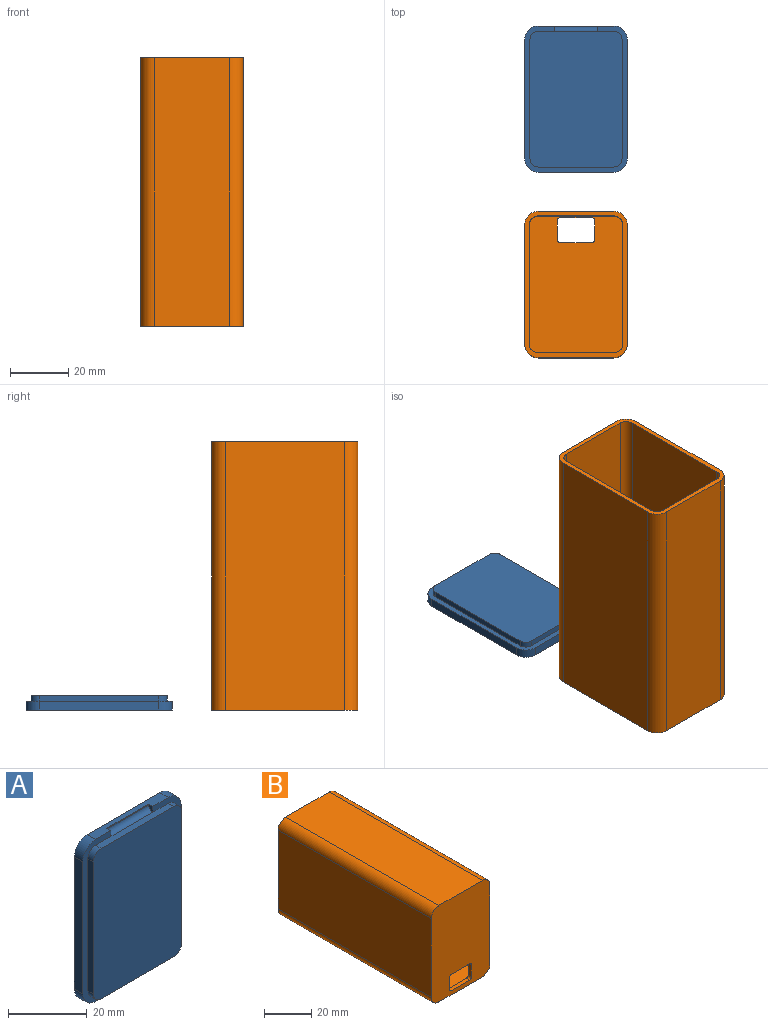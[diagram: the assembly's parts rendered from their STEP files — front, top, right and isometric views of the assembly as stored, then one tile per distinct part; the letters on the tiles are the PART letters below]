
ASSEMBLY  parts=2 mates=2
PART A: 23 faces, bbox 35.2x5x50.2 mm
  f0: plane 50.2x35.2mm, normal (0,-1,0), area 256mm2, adj f1,f2,f3,f4,f5,f6,f7,f8
  f1: plane 26x3mm, normal (0,0,1), area 55.5mm2, adj f0,f2,f8,f9,f19,f20,f21
  f2: cylinder r=4.6mm len=4.6mm, axis (0,-1,0), area 21.7mm2, adj f0,f1,f3,f9
  f3: plane 41x3mm, normal (1,0,0), area 123mm2, adj f0,f2,f4,f9
  f4: cylinder r=4.6mm len=4.6mm, axis (0,-1,0), area 21.7mm2, adj f0,f3,f5,f9
  f5: plane 26x3mm, normal (0,0,-1), area 78mm2, adj f0,f4,f6,f9
  f6: cylinder r=4.6mm len=4.6mm, axis (0,-1,0), area 21.7mm2, adj f0,f5,f7,f9
  f7: plane 41x3mm, normal (-1,0,0), area 123mm2, adj f0,f6,f8,f9
  f8: cylinder r=4.6mm len=4.6mm, axis (0,-1,0), area 21.7mm2, adj f0,f1,f7,f9
  f9: plane 50.2x35.2mm, normal (0,1,0), area 1748.9mm2, adj f1,f2,f3,f4,f5,f6,f7,f8
  f10: plane 41x2mm, normal (1,0,0), area 82mm2, adj f0,f11,f17,f18
  f11: cylinder r=2.8mm len=2.8mm, axis (0,1,0), area 8.8mm2, adj f0,f10,f12,f18
  f12: plane 26x2mm, normal (0,0,-1), area 52mm2, adj f0,f11,f13,f18
  f13: cylinder r=2.8mm len=2.8mm, axis (0,1,0), area 8.8mm2, adj f0,f12,f14,f18
  f14: plane 41x2mm, normal (-1,0,0), area 82mm2, adj f0,f13,f15,f18
  f15: cylinder r=2.8mm len=2.8mm, axis (0,1,0), area 8.8mm2, adj f0,f14,f16,f18
  f16: plane 26x2mm, normal (0,0,1), area 52mm2, adj f0,f15,f17,f18,f22
  f17: cylinder r=2.8mm len=2.8mm, axis (0,1,0), area 8.8mm2, adj f0,f10,f16,f18
  f18: plane 46.6x31.6mm, normal (0,-1,0), area 1465.8mm2, adj f10,f11,f12,f13,f14,f15,f16,f17
  f19: plane 1.8x1.5mm, normal (1,0,0), area 2.2mm2, adj f0,f1,f21,f22
  f20: plane 1.8x1.5mm, normal (-1,0,0), area 2.2mm2, adj f0,f1,f21,f22
  f21: plane 15x0.3mm, normal (0,-1,0), area 4.5mm2, adj f1,f19,f20,f22
  f22: cylinder r=1.5mm len=15mm, axis (1,0,0), area 35.3mm2, adj f16,f19,f20,f21
PART B: 27 faces, bbox 35.2x92x50.2 mm
  f0: plane 92x26mm, normal (0,0,1), area 2392mm2, adj f1,f15,f16,f25
  f1: cylinder r=4.6mm len=92mm, axis (0,-1,0), area 664.8mm2, adj f0,f2,f16,f25
  f2: plane 92x41mm, normal (-1,0,0), area 3772mm2, adj f1,f3,f16,f25
  f3: cylinder r=4.6mm len=92mm, axis (0,-1,0), area 664.8mm2, adj f2,f4,f16,f25
  f4: plane 92x26mm, normal (0,0,-1), area 2392mm2, adj f3,f5,f16,f25
  f5: cylinder r=4.6mm len=92mm, axis (0,-1,0), area 664.8mm2, adj f4,f6,f16,f25
  f6: plane 92x41mm, normal (1,0,0), area 3772mm2, adj f5,f15,f16,f25
  f7: cylinder r=3mm len=90mm, axis (0,-1,0), area 424.1mm2, adj f8,f14,f16,f26
  f8: plane 90x41mm, normal (-1,0,0), area 3690mm2, adj f7,f9,f16,f26
  f9: cylinder r=3mm len=90mm, axis (0,-1,0), area 424.1mm2, adj f8,f10,f16,f26
  f10: plane 90x26mm, normal (0,0,1), area 2340mm2, adj f9,f11,f16,f26
  f11: cylinder r=3mm len=90mm, axis (0,-1,0), area 424.1mm2, adj f10,f12,f16,f26
  f12: plane 90x41mm, normal (1,0,0), area 3690mm2, adj f11,f13,f16,f26
  f13: cylinder r=3mm len=90mm, axis (0,-1,0), area 424.1mm2, adj f12,f14,f16,f26
  f14: plane 90x26mm, normal (0,0,-1), area 2340mm2, adj f7,f13,f16,f26
  f15: cylinder r=4.6mm len=92mm, axis (0,-1,0), area 664.8mm2, adj f0,f6,f16,f25
  f16: plane 50.2x35.2mm, normal (0,1,0), area 252.6mm2, adj f0,f1,f2,f3,f4,f5,f6,f7
  f17: cylinder r=1mm len=2mm, axis (0,1,0), area 3.1mm2, adj f18,f24,f25,f26
  f18: plane 6.5x2mm, normal (1,0,0), area 13mm2, adj f17,f19,f25,f26
  f19: cylinder r=1mm len=2mm, axis (0,1,0), area 3.1mm2, adj f18,f20,f25,f26
  f20: plane 11x2mm, normal (0,0,-1), area 22mm2, adj f19,f21,f25,f26
  f21: cylinder r=1mm len=2mm, axis (0,1,0), area 3.1mm2, adj f20,f22,f25,f26
  f22: plane 6.5x2mm, normal (-1,0,0), area 13mm2, adj f21,f23,f25,f26
  f23: cylinder r=1mm len=2mm, axis (0,1,0), area 3.1mm2, adj f22,f24,f25,f26
  f24: plane 11x2mm, normal (0,0,1), area 22mm2, adj f17,f23,f25,f26
  f25: plane 50.2x35.2mm, normal (0,-1,0), area 1639.2mm2, adj f0,f1,f2,f3,f4,f5,f6,f15
  f26: plane 47x32mm, normal (0,1,0), area 1386.6mm2, adj f7,f8,f9,f10,f11,f12,f13,f14
PLACE A rot(axis=(-1,0,0),90deg) t=(0,98.8,86.41)mm
PLACE B rot(axis=(1,0,0),90deg) t=(0,35.05,-4.59)mm
MATE parallel B.f25 <-> A.f9  axis (0,0,-1) through (0,33.8,-6.59)mm
MATE parallel B.f25 <-> A.f9  axis (0,0,-1) through (0,33.8,-6.59)mm
